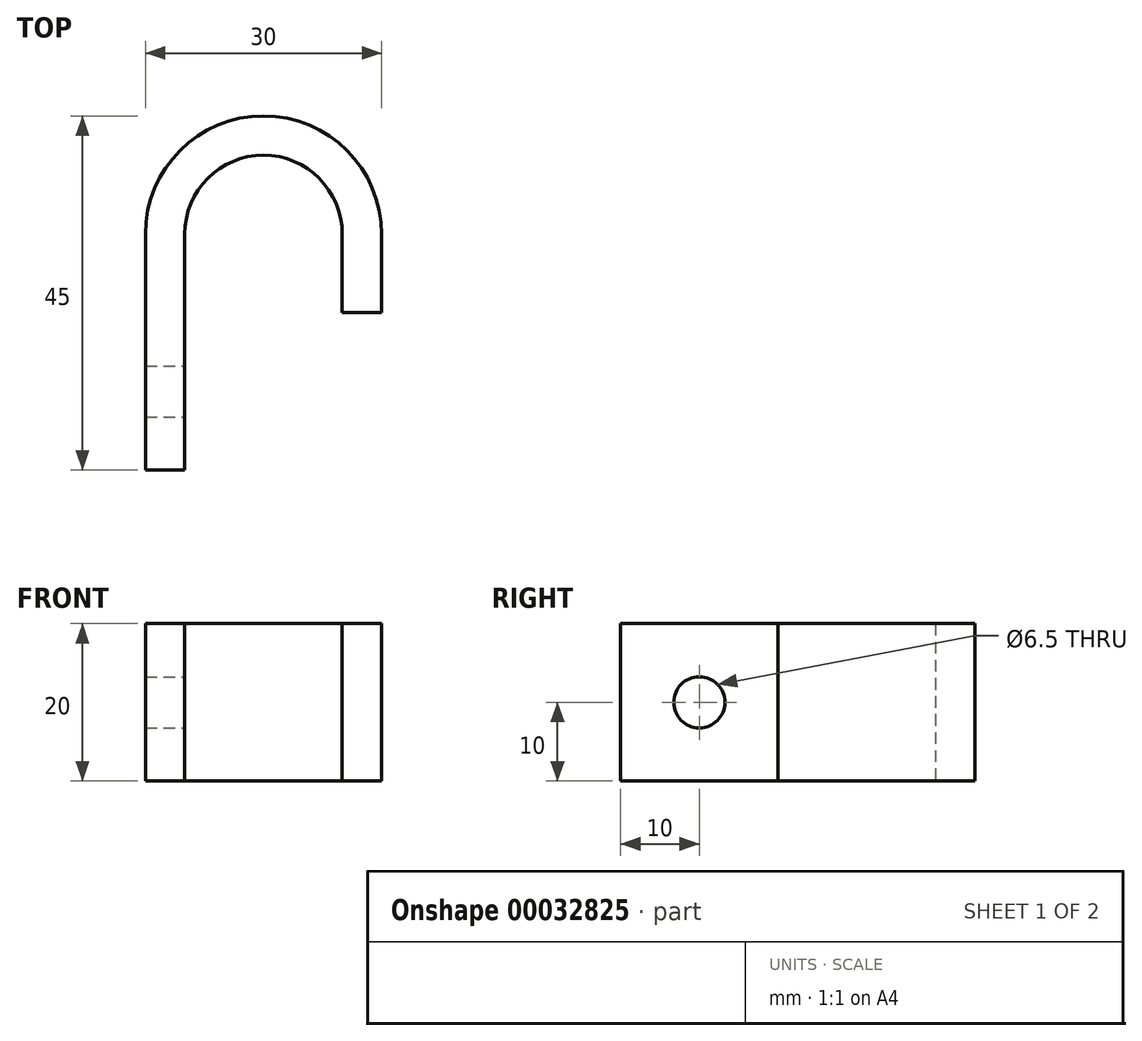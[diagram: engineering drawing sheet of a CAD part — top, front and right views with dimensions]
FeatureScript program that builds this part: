
annotation { "Feature Type Name" : "Feature", "Feature Type Description" : "" }
export const myFeature = defineFeature(function(context is Context, id is Id, definition is map)
    precondition{}
    {
        {
            var Q0;
            Q0=qCreatedBy(makeId("Top.planeOp"),FACE);
            var sketch = newSketch(context, id + "F0", { "sketchPlane" : qUnion([Q0])});
            skLineSegment(sketch, "E0", {"start": v(0, 0) * mm, "end": v(0, 10) * mm});
            skLineSegment(sketch, "E1", {"start": v(-15, 25) * mm, "end": v(-15, 25) * mm});
            skLineSegment(sketch, "E2", {"start": v(-30, 10) * mm, "end": v(-30, -20) * mm});
            skLineSegment(sketch, "E3.0", {"start": v(-25, 10) * mm, "end": v(-25, -20) * mm});
            skLineSegment(sketch, "E3.1", {"start": v(-15, 20) * mm, "end": v(-15, 20) * mm});
            skLineSegment(sketch, "E3.2", {"start": v(-5, 0) * mm, "end": v(-5, 10) * mm});
            skLineSegment(sketch, "E4", {"start": v(-30, -20) * mm, "end": v(-25, -20) * mm});
            skLineSegment(sketch, "E5", {"start": v(-5, 0) * mm, "end": v(0, 0) * mm});
            skPoint(sketch, "E6.visualSharp", {"position": v(-5, 20) * mm});
            skArc(sketch, "E6.filletArc", {"start": v(-5, 10) * mm, "mid": v(-7.93, 17.07) * mm, "end": v(-15, 20) * mm});
            skPoint(sketch, "E7.visualSharp", {"position": v(-25, 20) * mm});
            skArc(sketch, "E7.filletArc", {"start": v(-15, 20) * mm, "mid": v(-22.07, 17.07) * mm, "end": v(-25, 10) * mm});
            skPoint(sketch, "E8.visualSharp", {"position": v(-30, 25) * mm});
            skArc(sketch, "E8.filletArc", {"start": v(-15, 25) * mm, "mid": v(-25.6, 20.6) * mm, "end": v(-30, 10) * mm});
            skPoint(sketch, "E9.visualSharp", {"position": v(0, 25) * mm});
            skArc(sketch, "E9.filletArc", {"start": v(0, 10) * mm, "mid": v(-4.4, 20.6) * mm, "end": v(-15, 25) * mm});
            skSolve(sketch);
        }
        {
            var Q0;
            Q0=makeQuery(id+"F0.imprint","IMPRINT",FACE,{"disambiguationData":[TD([[makeQuery(id+"F0.imprint","IMPRINT",EDGE,{"derivedFrom":sQuery(id+"F0.wireOp",EDGE,"E0")}),1.0]])]});
            extrude(context, id + "F1", {"entities" : qUnion([Q0]), "depth" : 20 * mm});
        }
        {
            var Q0;
            Q0=makeQuery(id+"F1.opExtrude","SWEPT_FACE",FACE,{"disambiguationData":[OSD([sQuery(id+"F0.wireOp",EDGE,"E3.0")])]});
            var sketch = newSketch(context, id + "F2", { "sketchPlane" : qUnion([Q0])});
            skLineSegment(sketch, "E10.bottom", {"start": v(-20, 20) * mm, "end": v(0, 20) * mm});
            skLineSegment(sketch, "E10.top", {"start": v(-20, 0) * mm, "end": v(0, 0) * mm});
            skLineSegment(sketch, "E10.left", {"start": v(-20, 20) * mm, "end": v(-20, 0) * mm});
            skLineSegment(sketch, "E10.right", {"start": v(0, 20) * mm, "end": v(0, 0) * mm});
            skLineSegment(sketch, "E11", {"start": v(-20, 20) * mm, "end": v(0, 0) * mm});
            skCircle(sketch, "E12", {"center": v(-10, 10) * mm, "radius": 3.25 * mm});
            skSolve(sketch);
        }
        {
            var Q0;
            {var subQ0=sQuery(id+"F2.wireOp",EDGE,"E12");var subQ1=sQuery(id+"F2.wireOp",EDGE,"E11");var subQ3=makeQuery(id+"F2.imprint","INTERSECT",VERTEX,{"disambiguationData":[OD(0.0)],"derivedFrom":[subQ1,subQ0]});Q0=makeQuery(id+"F2.imprint","IMPRINT",FACE,{"disambiguationData":[TD([[makeQuery(id+"F2.imprint","IMPRINT",EDGE,{"disambiguationData":[TD([[subQ3,-1.0]])],"derivedFrom":subQ1}),1.0]])]});}
            var Q1;
            {var subQ0=sQuery(id+"F2.wireOp",EDGE,"E12");var subQ1=sQuery(id+"F2.wireOp",EDGE,"E11");var subQ3=makeQuery(id+"F2.imprint","INTERSECT",VERTEX,{"disambiguationData":[OD(0.0)],"derivedFrom":[subQ1,subQ0]});Q1=makeQuery(id+"F2.imprint","IMPRINT",FACE,{"disambiguationData":[TD([[makeQuery(id+"F2.imprint","IMPRINT",EDGE,{"disambiguationData":[TD([[subQ3,-1.0]])],"derivedFrom":subQ1}),-1.0]])]});}
            var Q2;
            Q2=sQuery(id+"F2.wireOp",EDGE,"E12");
            extrude(context, id + "F3", {"entities" : qUnion([Q0, Q1]), "operationType" : NewBodyOperationType.REMOVE, "surfaceEntities" : qUnion([Q2]), "oppositeDirection" : true, "depth" : 25 * mm});
        }
    });
